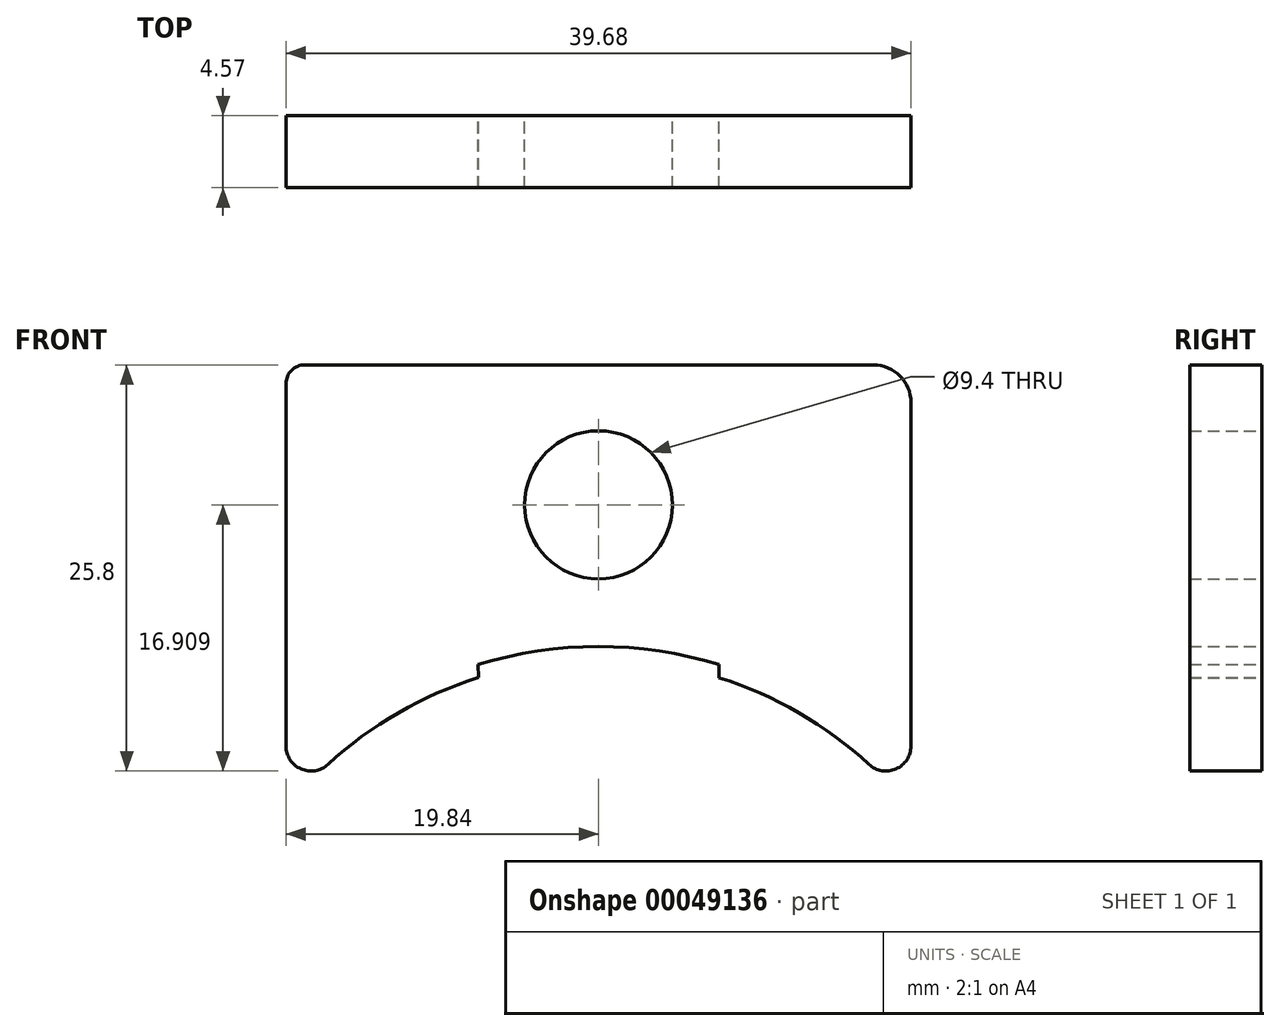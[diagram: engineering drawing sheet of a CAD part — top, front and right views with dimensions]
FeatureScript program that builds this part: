
annotation { "Feature Type Name" : "Feature", "Feature Type Description" : "" }
export const myFeature = defineFeature(function(context is Context, id is Id, definition is map)
    precondition{}
    {
        {
            var Q0;
            Q0=qCreatedBy(makeId("Front.planeOp"),FACE);
            var sketch = newSketch(context, id + "F0", { "sketchPlane" : qUnion([Q0])});
            skLineSegment(sketch, "E0.bottom", {"start": v(-18.65, 25.9) * mm, "end": v(17.46, 25.9) * mm});
            skLineSegment(sketch, "E0.top", {"start": v(-19.84, -2.24) * mm, "end": v(19.84, -2.24) * mm, "construction": true});
            skLineSegment(sketch, "E0.left", {"start": v(-19.84, 24.72) * mm, "end": v(-19.84, 1.7) * mm});
            skLineSegment(sketch, "E0.right", {"start": v(19.84, 23.53) * mm, "end": v(19.84, 1.7) * mm});
            skPoint(sketch, "E1", {"position": v(0, -18.18) * mm});
            skArc(sketch, "E2", {"start": v(-17.18, 0.53) * mm, "mid": v(-12.71, 3.81) * mm, "end": v(-7.63, 6.05) * mm});
            skArc(sketch, "E3", {"start": v(-7.66, 6.87) * mm, "mid": v(0, 8.02) * mm, "end": v(7.66, 6.87) * mm});
            skPoint(sketch, "E4.visualSharp", {"position": v(-19.84, 25.9) * mm});
            skArc(sketch, "E4.filletArc", {"start": v(-18.65, 25.9) * mm, "mid": v(-19.5, 25.56) * mm, "end": v(-19.84, 24.72) * mm});
            skPoint(sketch, "E5.visualSharp", {"position": v(19.84, 25.9) * mm});
            skArc(sketch, "E5.filletArc", {"start": v(19.84, 23.53) * mm, "mid": v(19.15, 25.21) * mm, "end": v(17.46, 25.9) * mm});
            skLineSegment(sketch, "E6", {"start": v(-7.66, 6.87) * mm, "end": v(0, -18.18) * mm, "construction": true});
            skLineSegment(sketch, "E7", {"start": v(7.66, 6.87) * mm, "end": v(0, -18.18) * mm, "construction": true});
            skLineSegment(sketch, "E8", {"start": v(0, 0) * mm, "end": v(0, -18.18) * mm, "construction": true});
            skLineSegment(sketch, "E9", {"start": v(0, -18.18) * mm, "end": v(19.84, -2.24) * mm, "construction": true});
            skLineSegment(sketch, "E10", {"start": v(-7.66, 6.87) * mm, "end": v(-7.63, 6.05) * mm});
            skArc(sketch, "E11", {"start": v(-7.63, 6.05) * mm, "mid": v(0.01, 7.22) * mm, "end": v(7.66, 6.04) * mm, "construction": true});
            skLineSegment(sketch, "E12", {"start": v(-7.63, 6.05) * mm, "end": v(-7.4, -2.24) * mm, "construction": true});
            skLineSegment(sketch, "E13", {"start": v(7.66, 6.87) * mm, "end": v(7.66, 6.04) * mm});
            skLineSegment(sketch, "E14", {"start": v(7.66, 6.04) * mm, "end": v(7.66, -2.24) * mm, "construction": true});
            skArc(sketch, "E15", {"start": v(7.66, 6.04) * mm, "mid": v(12.72, 3.8) * mm, "end": v(17.18, 0.53) * mm});
            skPoint(sketch, "E16.newPointA", {"position": v(-19.84, 0.5) * mm});
            skArc(sketch, "E16.filletArc", {"start": v(-19.84, 1.7) * mm, "mid": v(-18.9, 0.25) * mm, "end": v(-17.18, 0.53) * mm});
            skArc(sketch, "E17.filletArc", {"start": v(17.18, 0.53) * mm, "mid": v(18.9, 0.25) * mm, "end": v(19.84, 1.7) * mm});
            skCircle(sketch, "E18", {"center": v(0, 17.02) * mm, "radius": 4.7 * mm});
            skSolve(sketch);
        }
        {
            var Q0;
            Q0=makeQuery(id+"F0.imprint","IMPRINT",FACE,{"disambiguationData":[TD([[makeQuery(id+"F0.imprint","IMPRINT",EDGE,{"derivedFrom":sQuery(id+"F0.wireOp",EDGE,"E0.bottom")}),-1.0]])]});
            extrude(context, id + "F1", {"entities" : qUnion([Q0]), "depth" : 4.57 * mm});
        }
    });
